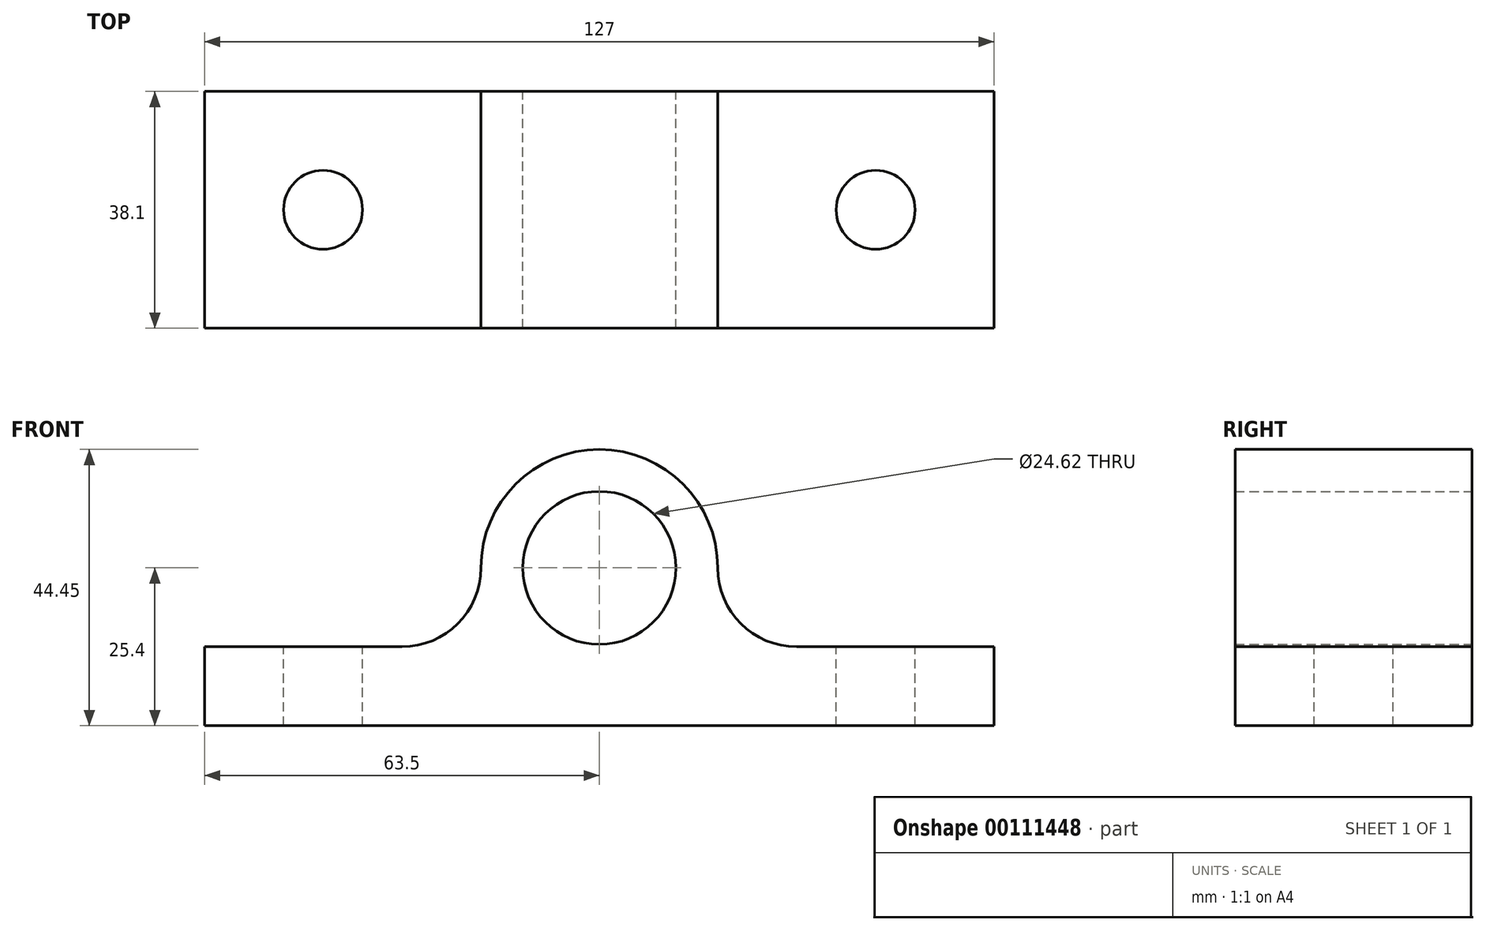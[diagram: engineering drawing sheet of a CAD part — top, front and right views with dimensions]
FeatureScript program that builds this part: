
annotation { "Feature Type Name" : "Feature", "Feature Type Description" : "" }
export const myFeature = defineFeature(function(context is Context, id is Id, definition is map)
    precondition{}
    {
        {
            var Q0;
            Q0=qCreatedBy(makeId("Front.planeOp"),FACE);
            var sketch = newSketch(context, id + "F0", { "sketchPlane" : qUnion([Q0])});
            skLineSegment(sketch, "E0", {"start": v(-127, 0) * mm, "end": v(0, 0) * mm});
            skLineSegment(sketch, "E1", {"start": v(0, 0) * mm, "end": v(0, 12.7) * mm});
            skLineSegment(sketch, "E2", {"start": v(-127, 12.7) * mm, "end": v(-127, 0) * mm});
            skLineSegment(sketch, "E3", {"start": v(-127, 12.7) * mm, "end": v(-102.2, 12.7) * mm});
            skLineSegment(sketch, "E4", {"start": v(-24.8, 12.7) * mm, "end": v(0, 12.7) * mm});
            skLineSegment(sketch, "E5", {"start": v(-102.2, 12.7) * mm, "end": v(-95.25, 12.7) * mm});
            skLineSegment(sketch, "E6", {"start": v(-31.75, 12.7) * mm, "end": v(-24.8, 12.7) * mm});
            skPoint(sketch, "E7.visualSharp", {"position": v(-82.55, 12.7) * mm});
            skArc(sketch, "E7.filletArc", {"start": v(-95.25, 12.7) * mm, "mid": v(-86.27, 16.42) * mm, "end": v(-82.55, 25.4) * mm});
            skPoint(sketch, "E8.visualSharp", {"position": v(-44.45, 12.7) * mm});
            skArc(sketch, "E8.filletArc", {"start": v(-44.45, 25.4) * mm, "mid": v(-40.73, 16.42) * mm, "end": v(-31.75, 12.7) * mm});
            skLineSegment(sketch, "E9", {"start": v(-63.5, 0) * mm, "end": v(-63.5, 25.4) * mm});
            skCircle(sketch, "E10", {"center": v(-63.5, 25.4) * mm, "radius": 12.31 * mm});
            skArc(sketch, "E11", {"start": v(-44.45, 25.4) * mm, "mid": v(-63.5, 44.45) * mm, "end": v(-82.55, 25.4) * mm});
            skSolve(sketch);
        }
        {
            var Q0;
            {var subQ3=sQuery(id+"F0.wireOp",EDGE,"E1");Q0=makeQuery(id+"F0.imprint","IMPRINT",FACE,{"disambiguationData":[TD([[makeQuery(id+"F0.imprint","IMPRINT",EDGE,{"derivedFrom":subQ3}),1.0]])]});}
            extrude(context, id + "F1", {"entities" : qUnion([Q0]), "depth" : 38.1 * mm});
        }
        {
            var Q0;
            Q0=makeQuery(id+"F1.opExtrude","SWEPT_FACE",FACE,{"disambiguationData":[OSD([sQuery(id+"F0.wireOp",EDGE,"E3"),sQuery(id+"F0.wireOp",EDGE,"E5")])]});
            var sketch = newSketch(context, id + "F2", { "sketchPlane" : qUnion([Q0])});
            skCircle(sketch, "E12", {"center": v(-107.95, -19.05) * mm, "radius": 6.35 * mm});
            skCircle(sketch, "E13", {"center": v(-19.05, -19.05) * mm, "radius": 6.35 * mm});
            skSolve(sketch);
        }
        {
            var Q0;
            Q0=makeQuery(id+"F2.imprint","IMPRINT",FACE,{"disambiguationData":[TD([[makeQuery(id+"F2.imprint","IMPRINT",EDGE,{"derivedFrom":sQuery(id+"F2.wireOp",EDGE,"E12")}),1.0]])]});
            var Q1;
            Q1=makeQuery(id+"F2.imprint","IMPRINT",FACE,{"disambiguationData":[TD([[makeQuery(id+"F2.imprint","IMPRINT",EDGE,{"derivedFrom":sQuery(id+"F2.wireOp",EDGE,"E13")}),1.0]])]});
            var Q2;
            Q2=sQuery(id+"F2.wireOp",EDGE,"E12");
            var Q3;
            Q3=sQuery(id+"F2.wireOp",EDGE,"E13");
            var Q4;
            Q4=makeQuery(id+"F1.opExtrude","SWEPT_BODY",BODY,{"disambiguationData":[OSD([sQuery(id+"F0.wireOp",EDGE,"E0"),sQuery(id+"F0.wireOp",EDGE,"E1"),sQuery(id+"F0.wireOp",EDGE,"E2"),sQuery(id+"F0.wireOp",EDGE,"E3"),sQuery(id+"F0.wireOp",EDGE,"E4"),sQuery(id+"F0.wireOp",EDGE,"E5"),sQuery(id+"F0.wireOp",EDGE,"E6"),sQuery(id+"F0.wireOp",EDGE,"E7.filletArc"),sQuery(id+"F0.wireOp",EDGE,"E8.filletArc"),sQuery(id+"F0.wireOp",EDGE,"E10"),sQuery(id+"F0.wireOp",EDGE,"E11")])]});
            extrude(context, id + "F3", {"entities" : qUnion([Q0, Q1]), "surfaceEntities" : qUnion([Q2, Q3]), "endBound" : BoundingType.UP_TO_BODY, "oppositeDirection" : true, "endBoundEntityBody" : qUnion([Q4]), "depth" : 25.4 * mm});
        }
    });
